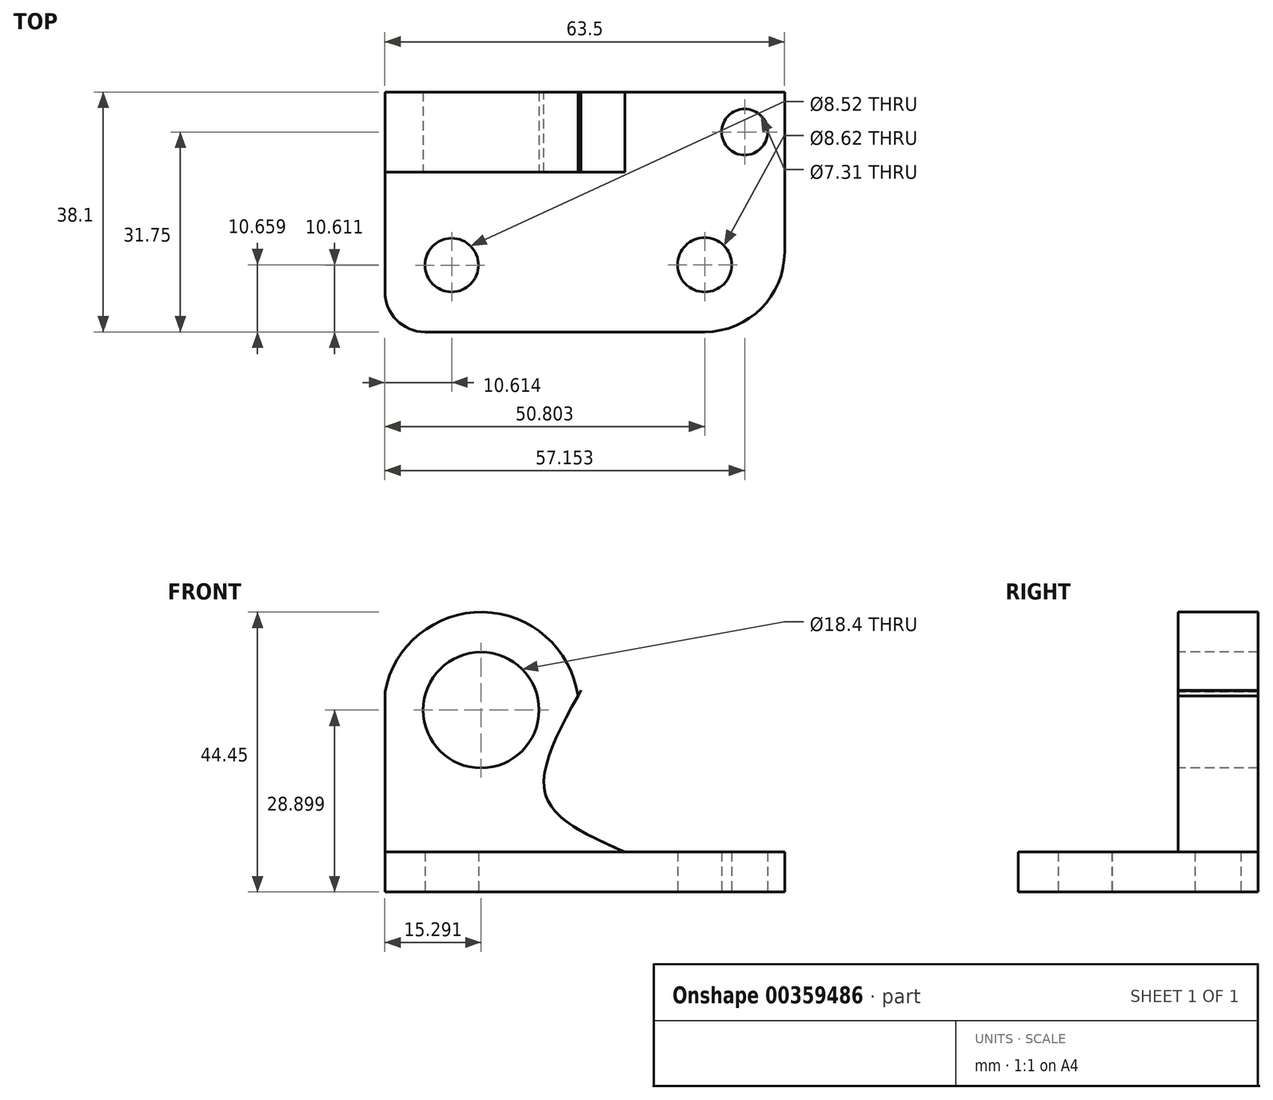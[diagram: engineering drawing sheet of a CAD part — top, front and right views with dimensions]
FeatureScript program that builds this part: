
annotation { "Feature Type Name" : "Feature", "Feature Type Description" : "" }
export const myFeature = defineFeature(function(context is Context, id is Id, definition is map)
    precondition{}
    {
        {
            var Q0;
            Q0=qCreatedBy(makeId("Front.planeOp"),FACE);
            var sketch = newSketch(context, id + "F0", { "sketchPlane" : qUnion([Q0])});
            skLineSegment(sketch, "E0", {"start": v(2.93, 33) * mm, "end": v(2.93, 26.65) * mm});
            skLineSegment(sketch, "E1", {"start": v(2.93, 26.65) * mm, "end": v(66.43, 26.65) * mm});
            skLineSegment(sketch, "E2", {"start": v(66.43, 26.65) * mm, "end": v(66.43, 33) * mm});
            skLineSegment(sketch, "E3", {"start": v(66.43, 33) * mm, "end": v(2.93, 33) * mm});
            skSolve(sketch);
        }
        {
            var Q0;
            Q0 = qSketchRegion(id + "F0", true);
            extrude(context, id + "F1", {"entities" : qUnion([Q0]), "oppositeDirection" : true, "depth" : 38.1 * mm});
        }
        {
            var Q0;
            Q0=makeQuery(id+"F1.opExtrude","SWEPT_FACE",FACE,{"disambiguationData":[OSD([sQuery(id+"F0.wireOp",EDGE,"E3")])]});
            var sketch = newSketch(context, id + "F2", { "sketchPlane" : qUnion([Q0])});
            skLineSegment(sketch, "E4", {"start": v(2.93, 38.1) * mm, "end": v(2.93, 25.4) * mm});
            skLineSegment(sketch, "E5", {"start": v(2.93, 25.4) * mm, "end": v(41.03, 25.4) * mm});
            skLineSegment(sketch, "E6", {"start": v(41.03, 25.4) * mm, "end": v(41.03, 38.1) * mm});
            skLineSegment(sketch, "E7", {"start": v(41.03, 38.1) * mm, "end": v(2.93, 38.1) * mm});
            skSolve(sketch);
        }
        {
            var Q0;
            Q0 = qSketchRegion(id + "F2", true);
            extrude(context, id + "F3", {"entities" : qUnion([Q0]), "operationType" : NewBodyOperationType.ADD, "depth" : 38.1 * mm});
        }
        {
            var Q0;
            Q0=makeQuery(id+"F3.opExtrude","SWEPT_FACE",FACE,{"disambiguationData":[OSD([sQuery(id+"F2.wireOp",EDGE,"E5")])]});
            var sketch = newSketch(context, id + "F4", { "sketchPlane" : qUnion([Q0])});
            skFitSpline(sketch, "E8", {"points": [v(41.03, 71.1) * mm, v(28.33, 42.62) * mm, v(41.03, 33) * mm], "startDerivative": vector(-32.67, -63.44) * mm, "endDerivative": vector(45.7, -20.62) * mm});
            skLineSegment(sketch, "E9", {"start": v(41.03, 71.1) * mm, "end": v(41.03, 33) * mm});
            skSolve(sketch);
        }
        {
            var Q0;
            Q0 = qSketchRegion(id + "F4", true);
            extrude(context, id + "F5", {"entities" : qUnion([Q0]), "operationType" : NewBodyOperationType.REMOVE, "oppositeDirection" : true, "depth" : 25.4 * mm});
        }
        {
            var Q0;
            Q0=makeQuery(id+"F3.opExtrude","SWEPT_FACE",FACE,{"disambiguationData":[OSD([sQuery(id+"F2.wireOp",EDGE,"E5")])]});
            var sketch = newSketch(context, id + "F6", { "sketchPlane" : qUnion([Q0])});
            skArc(sketch, "E10", {"start": v(33.61, 57.8) * mm, "mid": v(18.53, 71.1) * mm, "end": v(2.93, 58.4) * mm});
            skLineSegment(sketch, "E11", {"start": v(2.93, 58.4) * mm, "end": v(2.93, 71.1) * mm});
            skLineSegment(sketch, "E12", {"start": v(2.93, 71.1) * mm, "end": v(41.03, 71.1) * mm});
            skLineSegment(sketch, "E13", {"start": v(41.03, 71.1) * mm, "end": v(33.61, 57.8) * mm});
            skSolve(sketch);
        }
        {
            var Q0;
            Q0 = qSketchRegion(id + "F6", true);
            extrude(context, id + "F7", {"entities" : qUnion([Q0]), "operationType" : NewBodyOperationType.REMOVE, "oppositeDirection" : true, "depth" : 25.4 * mm});
        }
        {
            var Q0;
            Q0=qCreatedBy(makeId("Front.planeOp"),FACE);
            var sketch = newSketch(context, id + "F8", { "sketchPlane" : qUnion([Q0])});
            skLineSegment(sketch, "E14", {"start": v(31.45, 70.34) * mm, "end": v(35.18, 53.83) * mm});
            skLineSegment(sketch, "E15", {"start": v(35.18, 53.83) * mm, "end": v(52.08, 57.66) * mm});
            skLineSegment(sketch, "E16", {"start": v(52.08, 57.66) * mm, "end": v(43.59, 74.07) * mm});
            skLineSegment(sketch, "E17", {"start": v(43.59, 74.07) * mm, "end": v(31.45, 70.34) * mm});
            skSolve(sketch);
        }
        {
            var Q0;
            Q0 = qSketchRegion(id + "F8", true);
            extrude(context, id + "F9", {"entities" : qUnion([Q0]), "operationType" : NewBodyOperationType.REMOVE, "oppositeDirection" : true, "depth" : 50.8 * mm});
        }
        {
            var Q0;
            Q0=qCreatedBy(makeId("Front.planeOp"),FACE);
            var sketch = newSketch(context, id + "F10", { "sketchPlane" : qUnion([Q0])});
            skCircle(sketch, "E18", {"center": v(18.22, 55.55) * mm, "radius": 9.2 * mm});
            skSolve(sketch);
        }
        {
            var Q0;
            Q0 = qSketchRegion(id + "F10", true);
            extrude(context, id + "F11", {"entities" : qUnion([Q0]), "operationType" : NewBodyOperationType.REMOVE, "oppositeDirection" : true, "depth" : 50.8 * mm});
        }
        {
            var Q0;
            Q0=makeQuery(id+"F1.opExtrude","SWEPT_FACE",FACE,{"disambiguationData":[OSD([sQuery(id+"F0.wireOp",EDGE,"E3")])]});
            var sketch = newSketch(context, id + "F12", { "sketchPlane" : qUnion([Q0])});
            skLineSegment(sketch, "E19", {"start": v(2.93, 6.35) * mm, "end": v(2.93, 0) * mm});
            skLineSegment(sketch, "E20", {"start": v(2.93, 0) * mm, "end": v(9.28, 0) * mm});
            skArc(sketch, "E21", {"start": v(2.93, 6.35) * mm, "mid": v(4.8, 1.86) * mm, "end": v(9.28, 0) * mm});
            skLineSegment(sketch, "E22", {"start": v(66.43, 12.7) * mm, "end": v(66.43, 0) * mm});
            skLineSegment(sketch, "E23", {"start": v(66.43, 0) * mm, "end": v(53.73, 0) * mm});
            skArc(sketch, "E24", {"start": v(53.73, 0) * mm, "mid": v(62.71, 3.72) * mm, "end": v(66.43, 12.7) * mm});
            skSolve(sketch);
        }
        {
            var Q0;
            Q0 = qSketchRegion(id + "F12", true);
            extrude(context, id + "F13", {"entities" : qUnion([Q0]), "operationType" : NewBodyOperationType.REMOVE, "oppositeDirection" : true, "depth" : 25.4 * mm});
        }
        {
            var Q0;
            Q0=qCreatedBy(makeId("Top.planeOp"),FACE);
            var sketch = newSketch(context, id + "F14", { "sketchPlane" : qUnion([Q0])});
            skCircle(sketch, "E25", {"center": v(60.08, 31.75) * mm, "radius": 3.65 * mm});
            skCircle(sketch, "E26", {"center": v(53.73, 10.66) * mm, "radius": 4.3 * mm});
            skCircle(sketch, "E27", {"center": v(13.54, 10.61) * mm, "radius": 4.26 * mm});
            skSolve(sketch);
        }
        {
            var Q0;
            Q0 = qSketchRegion(id + "F14", true);
            extrude(context, id + "F15", {"entities" : qUnion([Q0]), "operationType" : NewBodyOperationType.REMOVE, "depth" : 50.8 * mm});
        }
    });
